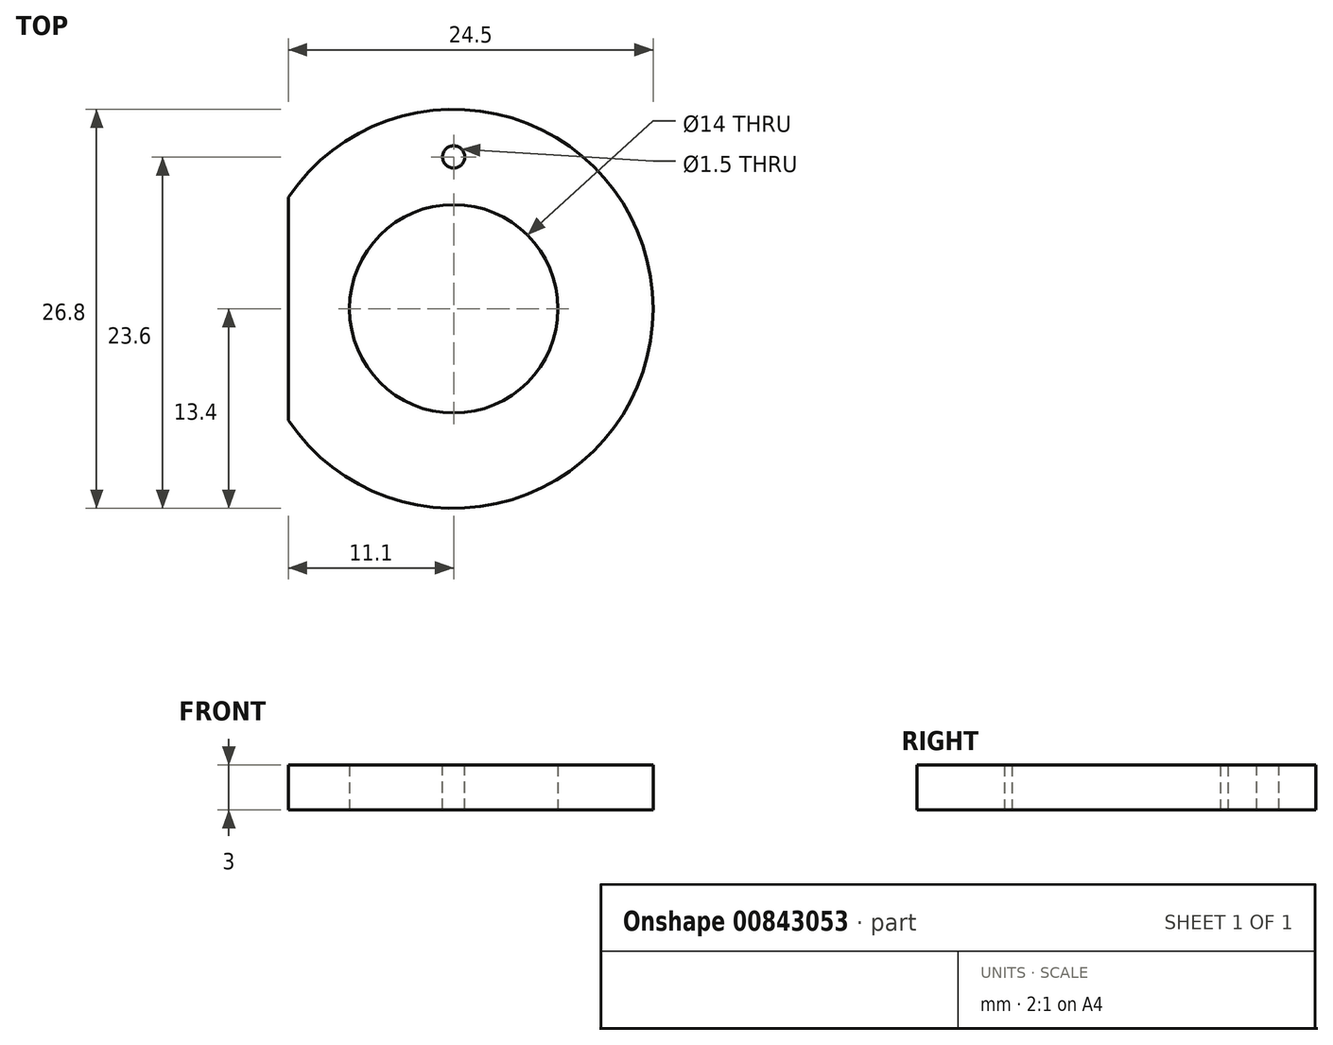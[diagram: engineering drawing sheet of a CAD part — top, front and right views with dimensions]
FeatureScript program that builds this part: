
annotation { "Feature Type Name" : "Feature", "Feature Type Description" : "" }
export const myFeature = defineFeature(function(context is Context, id is Id, definition is map)
    precondition{}
    {
        {
            var Q0;
            Q0=qCreatedBy(makeId("Top.planeOp"),FACE);
            var sketch = newSketch(context, id + "F0", { "sketchPlane" : qUnion([Q0])});
            skArc(sketch, "E0", {"start": v(-11.1, -7.5) * mm, "mid": v(13.4, 0) * mm, "end": v(-11.1, 7.5) * mm});
            skCircle(sketch, "E1", {"center": v(0, 0) * mm, "radius": 7 * mm});
            skLineSegment(sketch, "E2", {"start": v(-11.1, 7.5) * mm, "end": v(-11.1, -7.5) * mm});
            skSolve(sketch);
        }
        {
            var Q0;
            Q0=makeQuery(id+"F0.imprint","IMPRINT",FACE,{"disambiguationData":[TD([[makeQuery(id+"F0.imprint","IMPRINT",EDGE,{"derivedFrom":sQuery(id+"F0.wireOp",EDGE,"E1")}),-1.0]])]});
            extrude(context, id + "F1", {"entities" : qUnion([Q0]), "depth" : 3 * mm, "offsetDistance" : 25 * mm});
        }
        {
            var Q0;
            Q0=makeQuery(id+"F1.opExtrude","CAP_FACE",FACE,{"disambiguationData":[OSD([sQuery(id+"F0.wireOp",EDGE,"E0"),sQuery(id+"F0.wireOp",EDGE,"E1")])],"isStart":false});
            var sketch = newSketch(context, id + "F2", { "sketchPlane" : qUnion([Q0])});
            skCircle(sketch, "E3", {"center": v(0, 10.2) * mm, "radius": 0.75 * mm});
            skSolve(sketch);
        }
        {
            var Q0;
            Q0=makeQuery(id+"F2.imprint","IMPRINT",FACE,{"disambiguationData":[TD([[makeQuery(id+"F2.imprint","IMPRINT",EDGE,{"derivedFrom":sQuery(id+"F2.wireOp",EDGE,"E3")}),1.0]])]});
            extrude(context, id + "F3", {"entities" : qUnion([Q0]), "operationType" : NewBodyOperationType.REMOVE, "endBound" : BoundingType.THROUGH_ALL, "oppositeDirection" : true, "depth" : 25 * mm, "offsetDistance" : 25 * mm});
        }
    });
